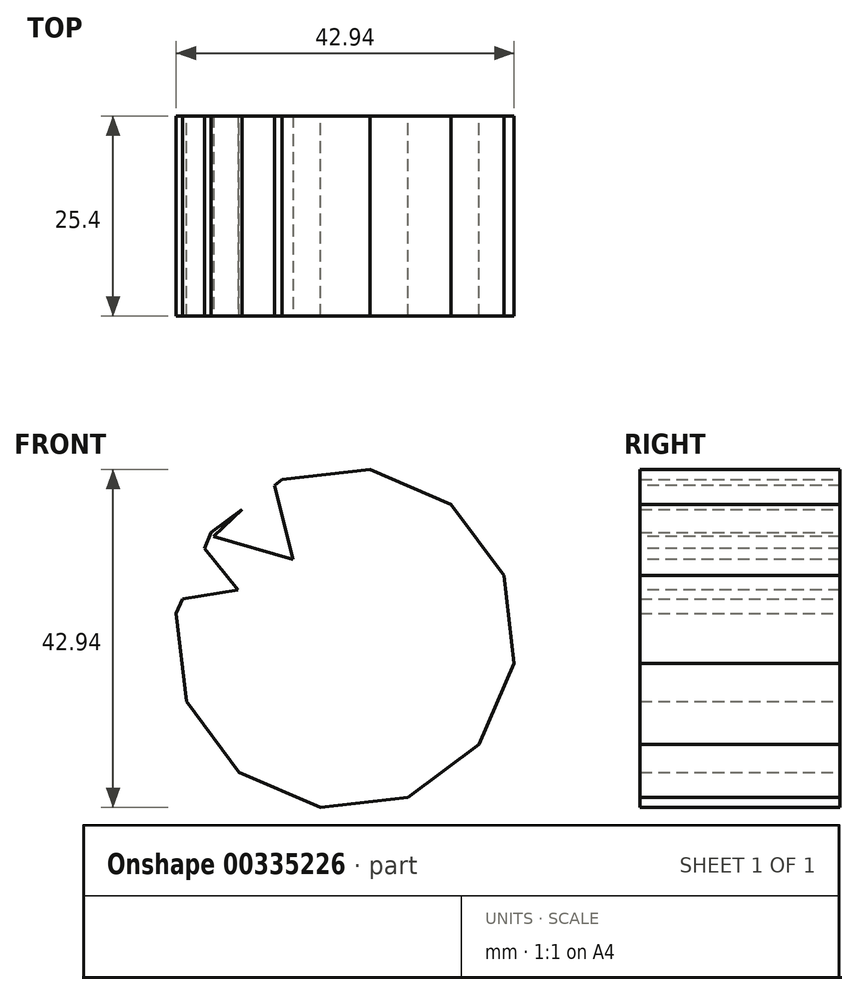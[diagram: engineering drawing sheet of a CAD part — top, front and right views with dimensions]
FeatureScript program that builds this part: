
annotation { "Feature Type Name" : "Feature", "Feature Type Description" : "" }
export const myFeature = defineFeature(function(context is Context, id is Id, definition is map)
    precondition{}
    {
        {
            var Q0;
            Q0=qCreatedBy(makeId("Front.planeOp"),FACE);
            var sketch = newSketch(context, id + "F0", { "sketchPlane" : qUnion([Q0])});
            skCircle(sketch, "E0.cCircle", {"center": v(-22.8, 7.45) * mm, "radius": 20.96 * mm, "construction": true});
            skLineSegment(sketch, "E0.0", {"start": v(-9.33, 24.47) * mm, "end": v(-2.63, 15.45) * mm});
            skLineSegment(sketch, "E0.1", {"start": v(-2.63, 15.45) * mm, "end": v(-1.33, 4.3) * mm});
            skLineSegment(sketch, "E0.2", {"start": v(-1.33, 4.3) * mm, "end": v(-5.78, -6.02) * mm});
            skLineSegment(sketch, "E0.3", {"start": v(-5.78, -6.02) * mm, "end": v(-14.8, -12.72) * mm});
            skLineSegment(sketch, "E0.4", {"start": v(-14.8, -12.72) * mm, "end": v(-25.96, -14.02) * mm});
            skLineSegment(sketch, "E0.5", {"start": v(-25.96, -14.02) * mm, "end": v(-36.27, -9.56) * mm});
            skLineSegment(sketch, "E0.6", {"start": v(-36.27, -9.56) * mm, "end": v(-42.97, -0.55) * mm});
            skLineSegment(sketch, "E0.7", {"start": v(-42.97, -0.55) * mm, "end": v(-44.27, 10.61) * mm});
            skLineSegment(sketch, "E0.8", {"start": v(-44.27, 10.61) * mm, "end": v(-39.81, 20.92) * mm});
            skLineSegment(sketch, "E0.9", {"start": v(-39.81, 20.92) * mm, "end": v(-30.8, 27.62) * mm});
            skLineSegment(sketch, "E0.10", {"start": v(-30.8, 27.62) * mm, "end": v(-19.64, 28.92) * mm});
            skLineSegment(sketch, "E0.11", {"start": v(-19.64, 28.92) * mm, "end": v(-9.33, 24.47) * mm});
            skPoint(sketch, "E0.0.midPoint", {"position": v(-5.98, 19.96) * mm});
            skSolve(sketch);
        }
        {
            var Q0;
            Q0 = qSketchRegion(id + "F0", true);
            extrude(context, id + "F1", {"entities" : qUnion([Q0]), "depth" : 25.4 * mm});
        }
        {
            var Q0;
            Q0=makeQuery(id+"F1.opExtrude","CAP_FACE",FACE,{"disambiguationData":[OSD([sQuery(id+"F0.wireOp",EDGE,"E0.0"),sQuery(id+"F0.wireOp",EDGE,"E0.1"),sQuery(id+"F0.wireOp",EDGE,"E0.2"),sQuery(id+"F0.wireOp",EDGE,"E0.3"),sQuery(id+"F0.wireOp",EDGE,"E0.4"),sQuery(id+"F0.wireOp",EDGE,"E0.5"),sQuery(id+"F0.wireOp",EDGE,"E0.6"),sQuery(id+"F0.wireOp",EDGE,"E0.7"),sQuery(id+"F0.wireOp",EDGE,"E0.8"),sQuery(id+"F0.wireOp",EDGE,"E0.9"),sQuery(id+"F0.wireOp",EDGE,"E0.10"),sQuery(id+"F0.wireOp",EDGE,"E0.11")])],"isStart":false});
            var sketch = newSketch(context, id + "F2", { "sketchPlane" : qUnion([Q0])});
            skCircle(sketch, "E1.cCircle", {"center": v(-42.04, 15.77) * mm, "radius": 3.02 * mm, "construction": true});
            skLineSegment(sketch, "E1.0", {"start": v(-46.74, 11.97) * mm, "end": v(-42.98, 21.74) * mm});
            skLineSegment(sketch, "E1.1", {"start": v(-42.98, 21.74) * mm, "end": v(-36.4, 13.6) * mm});
            skLineSegment(sketch, "E1.2", {"start": v(-36.4, 13.6) * mm, "end": v(-46.74, 11.97) * mm});
            skPoint(sketch, "E1.0.midPoint", {"position": v(-44.86, 16.85) * mm});
            skSolve(sketch);
        }
        {
            var Q0;
            Q0 = qSketchRegion(id + "F2", true);
            extrude(context, id + "F3", {"entities" : qUnion([Q0]), "operationType" : NewBodyOperationType.REMOVE, "oppositeDirection" : true, "depth" : 25.4 * mm});
        }
        {
            var Q0;
            Q0=makeQuery(id+"F1.opExtrude","CAP_FACE",FACE,{"disambiguationData":[OSD([sQuery(id+"F0.wireOp",EDGE,"E0.0"),sQuery(id+"F0.wireOp",EDGE,"E0.1"),sQuery(id+"F0.wireOp",EDGE,"E0.2"),sQuery(id+"F0.wireOp",EDGE,"E0.3"),sQuery(id+"F0.wireOp",EDGE,"E0.4"),sQuery(id+"F0.wireOp",EDGE,"E0.5"),sQuery(id+"F0.wireOp",EDGE,"E0.6"),sQuery(id+"F0.wireOp",EDGE,"E0.7"),sQuery(id+"F0.wireOp",EDGE,"E0.8"),sQuery(id+"F0.wireOp",EDGE,"E0.9"),sQuery(id+"F0.wireOp",EDGE,"E0.10"),sQuery(id+"F0.wireOp",EDGE,"E0.11")])],"isStart":false});
            var sketch = newSketch(context, id + "F4", { "sketchPlane" : qUnion([Q0])});
            skCircle(sketch, "E2.cCircle", {"center": v(-33.61, 21.84) * mm, "radius": 3.02 * mm, "construction": true});
            skLineSegment(sketch, "E2.0", {"start": v(-39.48, 20.38) * mm, "end": v(-31.94, 27.64) * mm});
            skLineSegment(sketch, "E2.1", {"start": v(-31.94, 27.64) * mm, "end": v(-29.42, 17.48) * mm});
            skLineSegment(sketch, "E2.2", {"start": v(-29.42, 17.48) * mm, "end": v(-39.48, 20.38) * mm});
            skPoint(sketch, "E2.0.midPoint", {"position": v(-35.71, 24.01) * mm});
            skSolve(sketch);
        }
        {
            var Q0;
            Q0 = qSketchRegion(id + "F4", true);
            extrude(context, id + "F5", {"entities" : qUnion([Q0]), "operationType" : NewBodyOperationType.REMOVE, "oppositeDirection" : true, "depth" : 25.4 * mm});
        }
    });
